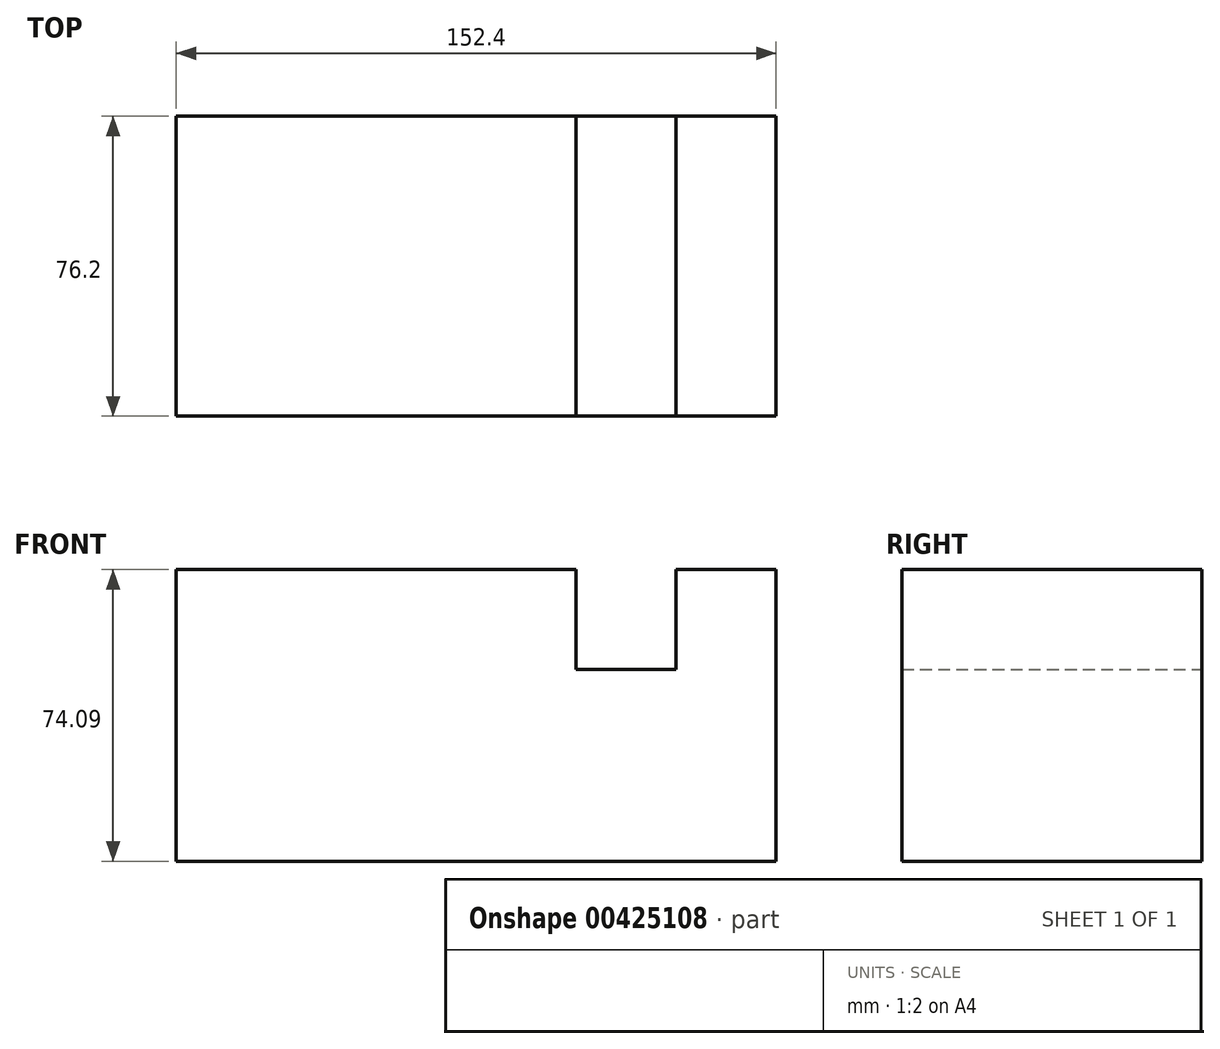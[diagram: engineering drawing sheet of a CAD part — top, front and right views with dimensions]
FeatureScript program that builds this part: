
annotation { "Feature Type Name" : "Feature", "Feature Type Description" : "" }
export const myFeature = defineFeature(function(context is Context, id is Id, definition is map)
    precondition{}
    {
        {
            var Q0;
            Q0=qCreatedBy(makeId("Front.planeOp"),FACE);
            var sketch = newSketch(context, id + "F0", { "sketchPlane" : qUnion([Q0])});
            skLineSegment(sketch, "E0", {"start": v(0, 0) * mm, "end": v(152.4, 0) * mm});
            skLineSegment(sketch, "E1", {"start": v(152.4, 0) * mm, "end": v(152.4, 74.09) * mm});
            skLineSegment(sketch, "E2", {"start": v(152.4, 74.09) * mm, "end": v(127, 74.09) * mm});
            skLineSegment(sketch, "E3", {"start": v(127, 74.09) * mm, "end": v(127, 48.69) * mm});
            skLineSegment(sketch, "E4", {"start": v(127, 48.69) * mm, "end": v(101.6, 48.69) * mm});
            skLineSegment(sketch, "E5", {"start": v(101.6, 48.69) * mm, "end": v(101.6, 74.09) * mm});
            skLineSegment(sketch, "E6", {"start": v(101.6, 74.09) * mm, "end": v(0, 74.09) * mm});
            skLineSegment(sketch, "E7", {"start": v(0, 74.09) * mm, "end": v(0, 0) * mm});
            skSolve(sketch);
        }
        {
            var Q0;
            Q0 = qSketchRegion(id + "F0", true);
            extrude(context, id + "F1", {"entities" : qUnion([Q0]), "depth" : 76.2 * mm});
        }
    });
